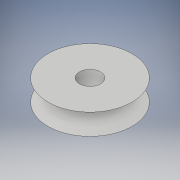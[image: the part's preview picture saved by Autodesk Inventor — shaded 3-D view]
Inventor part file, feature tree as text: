
AUTODESK INVENTOR PART (.ipt)
format: ipt  version: 2018 (Build 220112000, 112)  size: 112,128 bytes
history: native  units: in
note: dims shown in document units (in); Inventor stores cm internally (conversion verified against a paired STEP export)
features: extrude x3, sketch x3, chamfer x2
ambient origin geometry x8: Origin, YZ Plane, XZ Plane, XY Plane, X Axis, Y Axis, Z Axis, Center Point
bodies: Solid1 (feature_tree)
feature tree (8):
  extrude  "Extrusion1"  Depth=0.1in TaperAngle=0.0deg
  chamfer  "Chamfer1"  Distance=0.1in Angle=45.0deg
  extrude  "Extrusion2"  Depth=0.1in TaperAngle=45.0deg
  chamfer  "Chamfer2"  Distance=0.2in
  extrude  "Extrusion3"  [1 undecoded]
  sketch  "Sketch1"  dims[d0=0.8in d1=0.1in d2=0.0in d3=0.25in d4=0.1in d5=45.0deg]
  sketch  "Sketch2"  dims[d6=0.1in d7=0.0in d8=0.25in d9=0.1in d10=45.0deg]
  sketch  "Sketch3"  dims[d11=0.2in d12=0.2in d13=0.0in]
note: 1 required parameter value undecoded (feature->parameter linkage not recoverable at this tier; creation-order binding heuristic only, values carry confidence <= 0.55)
